# Revit family: rba-bim-rba4008 Series
name_source: partatom
category: Plumbing Fixtures
revit_build: Autodesk Revit 2018 (Build: 20170223_1515(x64)
units: mm (PartAtom-declared; Revit-internal decimal feet)

## family parameters
Always vertical = Yes
Cut with Voids When Loaded = No
Part Type = Normal
Room Calculation Point = No
Round Connector Dimension = Use Diameter
Shared = No
Work Plane-Based = No

## types (8) — shared parameters
Diameter = 32 mm  [stored 0.104987 ft]
Manufacturer = RBA Group
Materials and Finishes = Stainless Steel Bright Polished
Modified Issue = 20200316.01
URL = http://www.rba.com.au

## per-type parameters (varying)
| type | Lgth | Model |
| Straight Grab Rail 300mm | 300 mm | RBA4008-030 |
| Straight Grab Rail 450mm | 450 mm  [stored 1.47638 ft] | RBA4008-045 |
| Straight Grab Rail 600mm | 600 mm | RBA4008-060 |
| Straight Grab Rail 750mm | 750 mm  [stored 2.46063 ft] | RBA4008-075 |
| Straight Grab Rail 900mm | 900 mm  [stored 2.95276 ft] | RBA4008-090 |
| Straight Grab Rail 800mm | 800 mm  [stored 2.62467 ft] | RBA4008-080 |
| Straight Grab Rail 1000mm | 1000 mm  [stored 3.28084 ft] | RBA4008-100 |
| Straight Grab Rail 1200mm | 1200 mm | RBA4008-120 |

note: column(s) folded — value = type name in every type: Description

note: [stored X ft] marks values corroborated as IEEE doubles in the binary element streams (Revit-internal decimal feet)

## geometry (parser evidence)
native form markers: Blend x2, Sweep x3
no freeform markers — native parametric forms only
